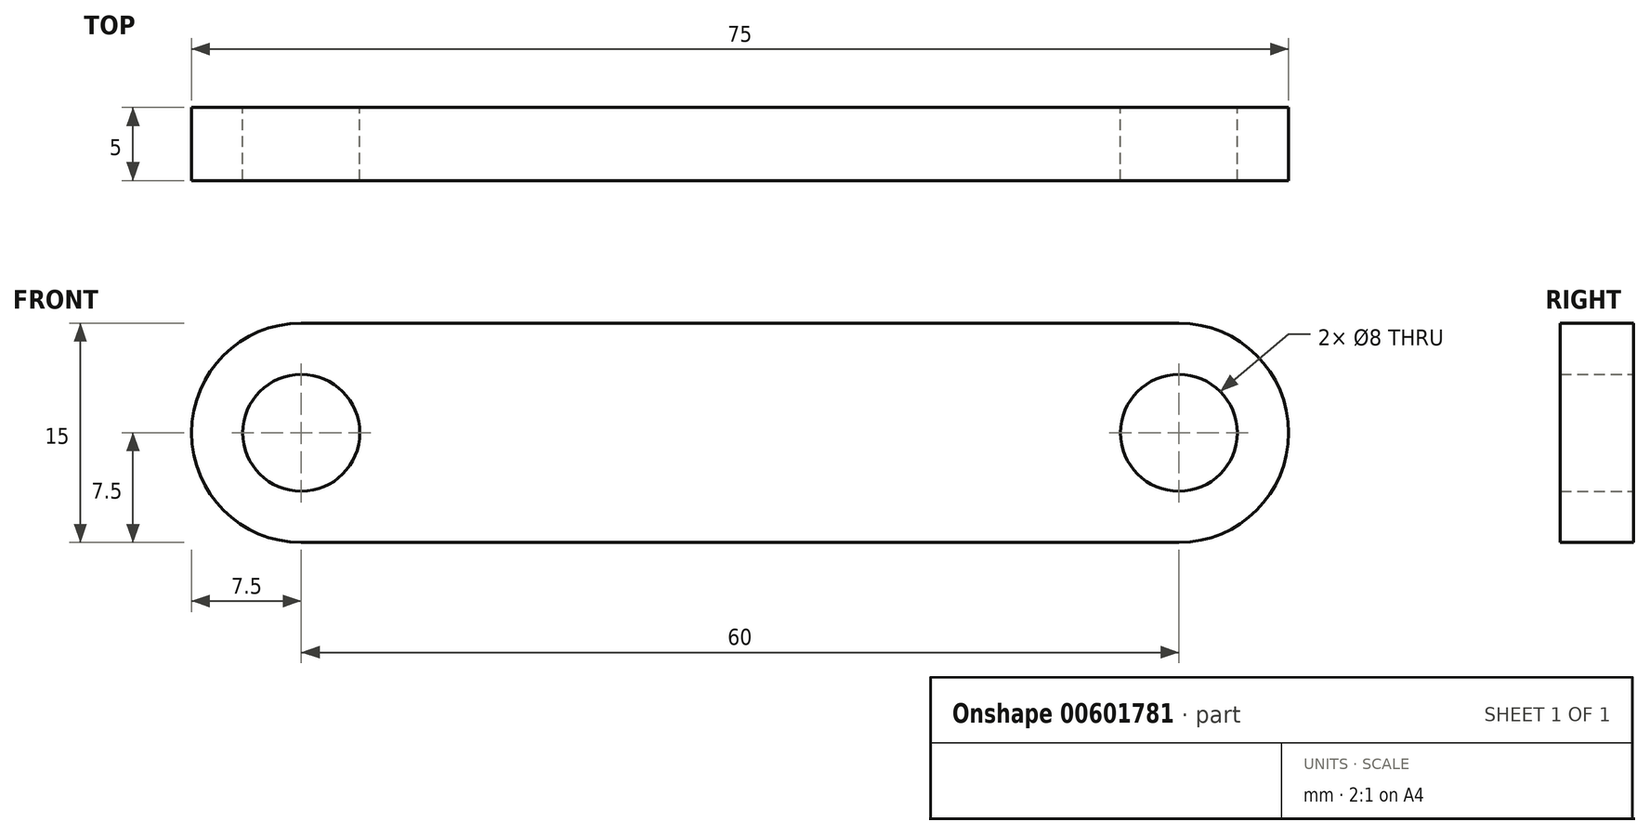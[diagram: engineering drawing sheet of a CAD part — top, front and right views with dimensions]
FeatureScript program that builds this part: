
annotation { "Feature Type Name" : "Feature", "Feature Type Description" : "" }
export const myFeature = defineFeature(function(context is Context, id is Id, definition is map)
    precondition{}
    {
        {
            var Q0;
            Q0=qCreatedBy(makeId("Front.planeOp"),FACE);
            var sketch = newSketch(context, id + "F0", { "sketchPlane" : qUnion([Q0])});
            skLineSegment(sketch, "E0", {"start": v(-30, 7.5) * mm, "end": v(30, 7.5) * mm});
            skLineSegment(sketch, "E1", {"start": v(-30, -7.5) * mm, "end": v(30, -7.5) * mm});
            skArc(sketch, "E2", {"start": v(30, -7.5) * mm, "mid": v(37.5, 0) * mm, "end": v(30, 7.5) * mm});
            skArc(sketch, "E3", {"start": v(-30, 7.5) * mm, "mid": v(-37.5, 0) * mm, "end": v(-30, -7.5) * mm});
            skCircle(sketch, "E4", {"center": v(-30, 0) * mm, "radius": 4 * mm});
            skCircle(sketch, "E5", {"center": v(30, 0) * mm, "radius": 4 * mm});
            skSolve(sketch);
        }
        {
            var Q0;
            Q0=makeQuery(id+"F0.imprint","IMPRINT",FACE,{"disambiguationData":[TD([[makeQuery(id+"F0.imprint","IMPRINT",EDGE,{"derivedFrom":sQuery(id+"F0.wireOp",EDGE,"E0")}),-1.0]])]});
            extrude(context, id + "F1", {"entities" : qUnion([Q0]), "depth" : 5 * mm, "offsetDistance" : 25 * mm});
        }
    });
